annotation { "Feature Type Name" : "Feature", "Feature Type Description" : "" }
export const myFeature = defineFeature(function(context is Context, id is Id, definition is map)
    precondition{}
    {
        {
            var Q0;
            Q0=qCreatedBy(makeId("Top.planeOp"),FACE);
            var sketch = newSketch(context, id + "F0", { "sketchPlane" : qUnion([Q0])});
            skLineSegment(sketch, "E0.bottom", {"start": v(-34.53, 54.72) * mm, "end": v(41.67, 54.72) * mm});
            skLineSegment(sketch, "E0.top", {"start": v(-34.53, -59.58) * mm, "end": v(41.67, -59.58) * mm});
            skLineSegment(sketch, "E0.left", {"start": v(-34.53, 54.72) * mm, "end": v(-34.53, -59.58) * mm});
            skLineSegment(sketch, "E0.right", {"start": v(41.67, 54.72) * mm, "end": v(41.67, -59.58) * mm});
            skSolve(sketch);
        }
        {
            var Q0;
            Q0 = qSketchRegion(id + "F0", true);
            extrude(context, id + "F1", {"entities" : qUnion([Q0]), "depth" : 3.17 * mm});
        }
        {
            var Q0;
            Q0=makeQuery(id+"F1.opExtrude","CAP_FACE",FACE,{"disambiguationData":[OSD([sQuery(id+"F0.wireOp",EDGE,"E0.bottom"),sQuery(id+"F0.wireOp",EDGE,"E0.top"),sQuery(id+"F0.wireOp",EDGE,"E0.left"),sQuery(id+"F0.wireOp",EDGE,"E0.right")])],"isStart":false});
            var sketch = newSketch(context, id + "F2", { "sketchPlane" : qUnion([Q0])});
            skText(sketch, "E1", { "text": "STEM STUDENTS", "fontName": "AllertaStencil-Regular.ttf"});
            const initialGuessF2  = {"E1": [-0.03511, 0.04116, 1, 0, 0.0069]};
            skSetInitialGuess(sketch, initialGuessF2);
            skSolve(sketch);
        }
        {
            var Q0;
            Q0 = qSketchRegion(id + "F2", true);
            extrude(context, id + "F3", {"entities" : qUnion([Q0]), "operationType" : NewBodyOperationType.REMOVE, "oppositeDirection" : true, "depth" : 3.17 * mm});
        }
        {
            var Q0;
            Q0=makeQuery(id+"F1.opExtrude","CAP_FACE",FACE,{"disambiguationData":[OSD([sQuery(id+"F0.wireOp",EDGE,"E0.bottom"),sQuery(id+"F0.wireOp",EDGE,"E0.top"),sQuery(id+"F0.wireOp",EDGE,"E0.left"),sQuery(id+"F0.wireOp",EDGE,"E0.right")])],"isStart":false});
            var sketch = newSketch(context, id + "F4", { "sketchPlane" : qUnion([Q0])});
            skText(sketch, "E2", { "text": "HALL PASS", "fontName": "AllertaStencil-Regular.ttf"});
            const initialGuessF4  = {"E2": [-0.0167, 0.0236, 1, 0, 0.0049]};
            skSetInitialGuess(sketch, initialGuessF4);
            skSolve(sketch);
        }
        {
            var Q0;
            Q0 = qSketchRegion(id + "F4", true);
            extrude(context, id + "F5", {"entities" : qUnion([Q0]), "operationType" : NewBodyOperationType.REMOVE, "oppositeDirection" : true, "depth" : 3.17 * mm});
        }
        {
            var Q0;
            Q0=makeQuery(id+"F1.opExtrude","CAP_FACE",FACE,{"disambiguationData":[OSD([sQuery(id+"F0.wireOp",EDGE,"E0.bottom"),sQuery(id+"F0.wireOp",EDGE,"E0.top"),sQuery(id+"F0.wireOp",EDGE,"E0.left"),sQuery(id+"F0.wireOp",EDGE,"E0.right")])],"isStart":false});
            var sketch = newSketch(context, id + "F6", { "sketchPlane" : qUnion([Q0])});
            skText(sketch, "E3", { "text": "Recycling", "fontName": "AllertaStencil-Regular.ttf"});
            const initialGuessF6  = {"E3": [-0.01353, 0.00547, 1, 0, 0.00374]};
            skSetInitialGuess(sketch, initialGuessF6);
            skSolve(sketch);
        }
        {
            var Q0;
            Q0 = qSketchRegion(id + "F6", true);
            extrude(context, id + "F7", {"entities" : qUnion([Q0]), "operationType" : NewBodyOperationType.REMOVE, "oppositeDirection" : true, "depth" : 3.17 * mm});
        }
        {
            var Q0;
            Q0=makeQuery(id+"F1.opExtrude","CAP_FACE",FACE,{"disambiguationData":[OSD([sQuery(id+"F0.wireOp",EDGE,"E0.bottom"),sQuery(id+"F0.wireOp",EDGE,"E0.top"),sQuery(id+"F0.wireOp",EDGE,"E0.left"),sQuery(id+"F0.wireOp",EDGE,"E0.right")])],"isStart":false});
            var sketch = newSketch(context, id + "F8", { "sketchPlane" : qUnion([Q0])});
            skLineSegment(sketch, "E4", {"start": v(0, -4.9) * mm, "end": v(-12.09, -18.42) * mm});
            skLineSegment(sketch, "E5", {"start": v(-12.09, -18.42) * mm, "end": v(10.07, -18.42) * mm});
            skLineSegment(sketch, "E6", {"start": v(10.07, -18.42) * mm, "end": v(0, -4.9) * mm});
            skLineSegment(sketch, "E7", {"start": v(-1, -21.3) * mm, "end": v(-12.38, -29.07) * mm});
            skPoint(sketch, "E7.startSnap0", {"position": v(-1, -18.42) * mm});
            skLineSegment(sketch, "E8", {"start": v(-12.38, -29.07) * mm, "end": v(12.38, -29.07) * mm});
            skLineSegment(sketch, "E9", {"start": v(12.38, -29.07) * mm, "end": v(-1, -21.3) * mm});
            skLineSegment(sketch, "E10.bottom", {"start": v(-3.17, -32.8) * mm, "end": v(3.45, -32.8) * mm});
            skLineSegment(sketch, "E10.top", {"start": v(-3.17, -44.32) * mm, "end": v(3.45, -44.32) * mm});
            skLineSegment(sketch, "E10.left", {"start": v(-3.17, -32.8) * mm, "end": v(-3.17, -44.32) * mm});
            skLineSegment(sketch, "E10.right", {"start": v(3.45, -32.8) * mm, "end": v(3.45, -44.32) * mm});
            skSolve(sketch);
        }
        {
            var Q0;
            Q0 = qSketchRegion(id + "F8", true);
            extrude(context, id + "F9", {"entities" : qUnion([Q0]), "operationType" : NewBodyOperationType.REMOVE, "oppositeDirection" : true, "depth" : 3.17 * mm});
        }
    });